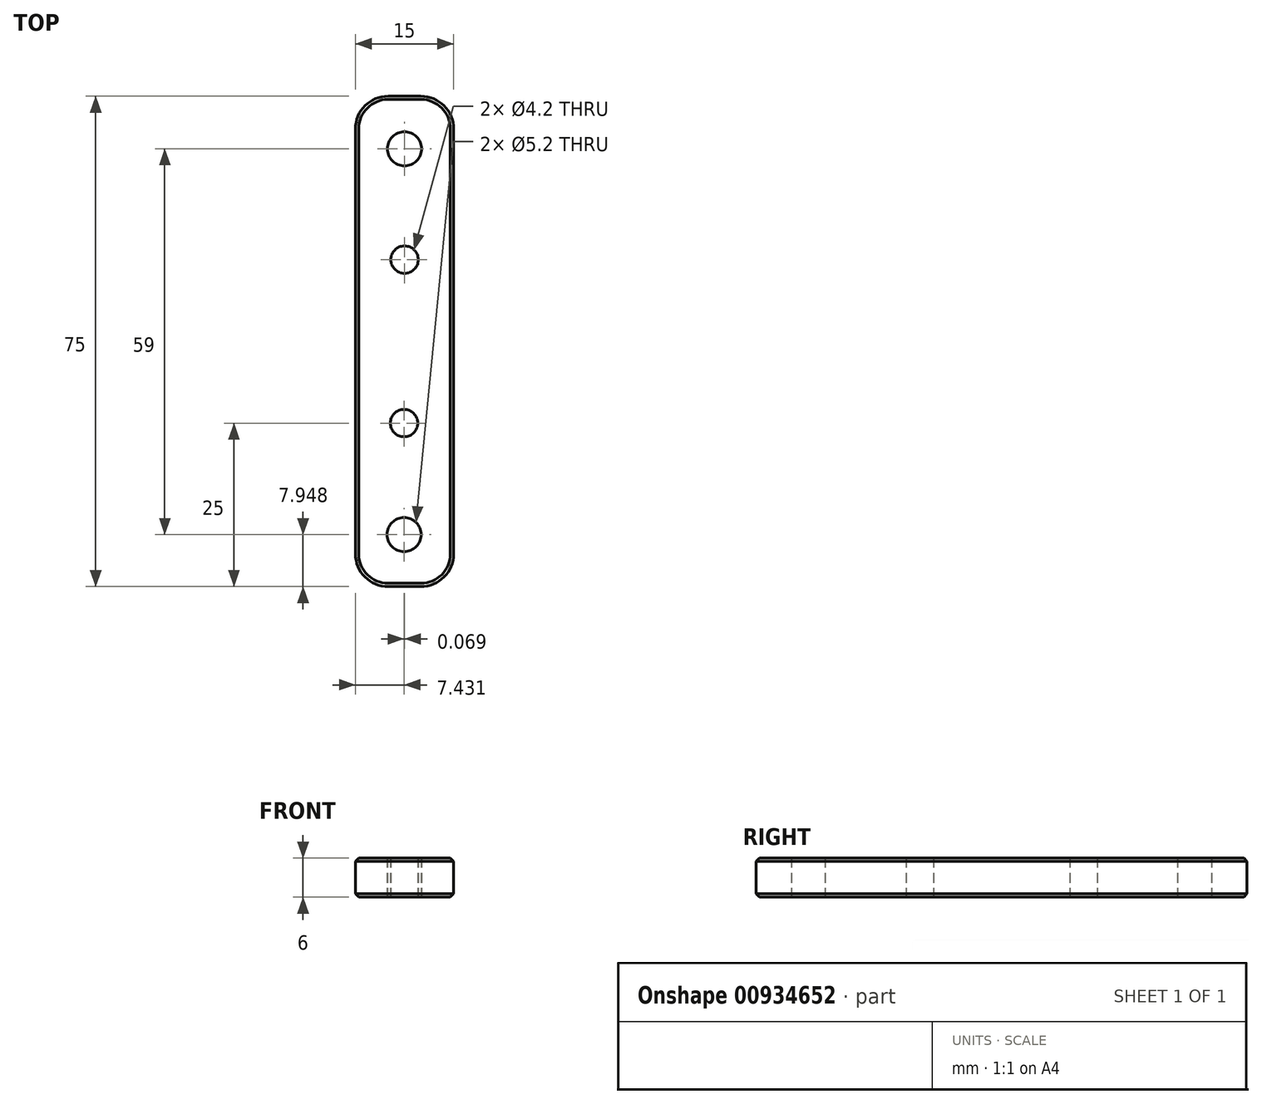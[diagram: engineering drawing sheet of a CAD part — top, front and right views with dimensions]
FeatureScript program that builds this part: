
annotation { "Feature Type Name" : "Feature", "Feature Type Description" : "" }
export const myFeature = defineFeature(function(context is Context, id is Id, definition is map)
    precondition{}
    {
        {
            var Q0;
            Q0=qCreatedBy(makeId("Top.planeOp"),FACE);
            var sketch = newSketch(context, id + "F0", { "sketchPlane" : qUnion([Q0])});
            skLineSegment(sketch, "E0.bottom", {"start": v(-7.5, 37.5) * mm, "end": v(7.5, 37.5) * mm});
            skLineSegment(sketch, "E0.top", {"start": v(-7.5, -37.5) * mm, "end": v(7.5, -37.5) * mm});
            skLineSegment(sketch, "E0.left", {"start": v(-7.5, 37.5) * mm, "end": v(-7.5, -37.5) * mm});
            skLineSegment(sketch, "E0.right", {"start": v(7.5, 37.5) * mm, "end": v(7.5, -37.5) * mm});
            skPoint(sketch, "E0.middle", {"position": v(0, 0) * mm});
            skCircle(sketch, "E1", {"center": v(0, 12.5) * mm, "radius": 2.1 * mm});
            skCircle(sketch, "E2", {"center": v(-0.07, -12.5) * mm, "radius": 2.1 * mm});
            skCircle(sketch, "E3", {"center": v(0, 29.45) * mm, "radius": 2.6 * mm});
            skCircle(sketch, "E4", {"center": v(-0.07, -29.55) * mm, "radius": 2.6 * mm});
            skSolve(sketch);
        }
        {
            var Q0;
            Q0=makeQuery(id+"F0.imprint","IMPRINT",FACE,{"disambiguationData":[TD([[makeQuery(id+"F0.imprint","IMPRINT",EDGE,{"derivedFrom":sQuery(id+"F0.wireOp",EDGE,"E0.bottom")}),-1.0]])]});
            extrude(context, id + "F1", {"entities" : qUnion([Q0]), "depth" : 6 * mm, "offsetDistance" : 25 * mm});
        }
        {
            var Q0;
            Q0=makeQuery(id+"F1.opExtrude","SWEPT_EDGE",EDGE,{"disambiguationData":[OSD([sQuery(id+"F0.wireOp",EDGE,"E0.bottom"),sQuery(id+"F0.wireOp",EDGE,"E0.left")])]});
            var Q1;
            Q1=makeQuery(id+"F1.opExtrude","SWEPT_EDGE",EDGE,{"disambiguationData":[OSD([sQuery(id+"F0.wireOp",EDGE,"E0.bottom"),sQuery(id+"F0.wireOp",EDGE,"E0.right")])]});
            var Q2;
            Q2=makeQuery(id+"F1.opExtrude","SWEPT_EDGE",EDGE,{"disambiguationData":[OSD([sQuery(id+"F0.wireOp",EDGE,"E0.top"),sQuery(id+"F0.wireOp",EDGE,"E0.left")])]});
            var Q3;
            Q3=makeQuery(id+"F1.opExtrude","SWEPT_EDGE",EDGE,{"disambiguationData":[OSD([sQuery(id+"F0.wireOp",EDGE,"E0.top"),sQuery(id+"F0.wireOp",EDGE,"E0.right")])]});
            fillet(context, id + "F2", {"entities" : qUnion([Q0, Q1, Q2, Q3]), "radius" : 5 * mm, "tangentPropagation" : true, "allowEdgeOverflow" : false});
        }
        {
            var Q0;
            Q0=makeQuery(id+"F1.opExtrude","CAP_EDGE",EDGE,{"disambiguationData":[OSD([sQuery(id+"F0.wireOp",EDGE,"E0.left")])],"isStart":false});
            var Q1;
            Q1=makeQuery(id+"F1.opExtrude","CAP_EDGE",EDGE,{"disambiguationData":[OSD([sQuery(id+"F0.wireOp",EDGE,"E0.right")])],"isStart":false});
            var Q2;
            {var subQ0=sQuery(id+"F0.wireOp",EDGE,"E0.right");var subQ1=sQuery(id+"F0.wireOp",EDGE,"E0.bottom");Q2=makeQuery(id+"F2.opFillet","BLEND_EDGE",EDGE,{"blendedFrom":[makeQuery(id+"F1.opExtrude","SWEPT_EDGE",EDGE,{"disambiguationData":[OSD([subQ1,subQ0])]}),makeQuery(id+"F1.opExtrude","CAP_FACE",FACE,{"disambiguationData":[OSD([subQ1,sQuery(id+"F0.wireOp",EDGE,"E0.top"),sQuery(id+"F0.wireOp",EDGE,"E0.left"),subQ0,sQuery(id+"F0.wireOp",EDGE,"E1"),sQuery(id+"F0.wireOp",EDGE,"E2"),sQuery(id+"F0.wireOp",EDGE,"E3"),sQuery(id+"F0.wireOp",EDGE,"E4")])],"isStart":false})],"blendedInto":[makeQuery(id+"F1.opExtrude","CAP_FACE",FACE,{"disambiguationData":[OSD([subQ1,sQuery(id+"F0.wireOp",EDGE,"E0.top"),sQuery(id+"F0.wireOp",EDGE,"E0.left"),subQ0,sQuery(id+"F0.wireOp",EDGE,"E1"),sQuery(id+"F0.wireOp",EDGE,"E2"),sQuery(id+"F0.wireOp",EDGE,"E3"),sQuery(id+"F0.wireOp",EDGE,"E4")])],"isStart":false})]});}
            var Q3;
            Q3=makeQuery(id+"F1.opExtrude","CAP_EDGE",EDGE,{"disambiguationData":[OSD([sQuery(id+"F0.wireOp",EDGE,"E0.bottom")])],"isStart":false});
            var Q4;
            {var subQ0=sQuery(id+"F0.wireOp",EDGE,"E0.left");var subQ1=sQuery(id+"F0.wireOp",EDGE,"E0.bottom");Q4=makeQuery(id+"F2.opFillet","BLEND_EDGE",EDGE,{"blendedFrom":[makeQuery(id+"F1.opExtrude","SWEPT_EDGE",EDGE,{"disambiguationData":[OSD([subQ1,subQ0])]}),makeQuery(id+"F1.opExtrude","CAP_FACE",FACE,{"disambiguationData":[OSD([subQ1,sQuery(id+"F0.wireOp",EDGE,"E0.top"),subQ0,sQuery(id+"F0.wireOp",EDGE,"E0.right"),sQuery(id+"F0.wireOp",EDGE,"E1"),sQuery(id+"F0.wireOp",EDGE,"E2"),sQuery(id+"F0.wireOp",EDGE,"E3"),sQuery(id+"F0.wireOp",EDGE,"E4")])],"isStart":false})],"blendedInto":[makeQuery(id+"F1.opExtrude","CAP_FACE",FACE,{"disambiguationData":[OSD([subQ1,sQuery(id+"F0.wireOp",EDGE,"E0.top"),subQ0,sQuery(id+"F0.wireOp",EDGE,"E0.right"),sQuery(id+"F0.wireOp",EDGE,"E1"),sQuery(id+"F0.wireOp",EDGE,"E2"),sQuery(id+"F0.wireOp",EDGE,"E3"),sQuery(id+"F0.wireOp",EDGE,"E4")])],"isStart":false})]});}
            var Q5;
            {var subQ0=sQuery(id+"F0.wireOp",EDGE,"E0.left");var subQ1=sQuery(id+"F0.wireOp",EDGE,"E0.top");Q5=makeQuery(id+"F2.opFillet","BLEND_EDGE",EDGE,{"blendedFrom":[makeQuery(id+"F1.opExtrude","SWEPT_EDGE",EDGE,{"disambiguationData":[OSD([subQ1,subQ0])]}),makeQuery(id+"F1.opExtrude","CAP_FACE",FACE,{"disambiguationData":[OSD([sQuery(id+"F0.wireOp",EDGE,"E0.bottom"),subQ1,subQ0,sQuery(id+"F0.wireOp",EDGE,"E0.right"),sQuery(id+"F0.wireOp",EDGE,"E1"),sQuery(id+"F0.wireOp",EDGE,"E2"),sQuery(id+"F0.wireOp",EDGE,"E3"),sQuery(id+"F0.wireOp",EDGE,"E4")])],"isStart":false})],"blendedInto":[makeQuery(id+"F1.opExtrude","CAP_FACE",FACE,{"disambiguationData":[OSD([sQuery(id+"F0.wireOp",EDGE,"E0.bottom"),subQ1,subQ0,sQuery(id+"F0.wireOp",EDGE,"E0.right"),sQuery(id+"F0.wireOp",EDGE,"E1"),sQuery(id+"F0.wireOp",EDGE,"E2"),sQuery(id+"F0.wireOp",EDGE,"E3"),sQuery(id+"F0.wireOp",EDGE,"E4")])],"isStart":false})]});}
            var Q6;
            Q6=makeQuery(id+"F1.opExtrude","CAP_EDGE",EDGE,{"disambiguationData":[OSD([sQuery(id+"F0.wireOp",EDGE,"E0.top")])],"isStart":false});
            var Q7;
            {var subQ0=sQuery(id+"F0.wireOp",EDGE,"E0.right");var subQ1=sQuery(id+"F0.wireOp",EDGE,"E0.top");Q7=makeQuery(id+"F2.opFillet","BLEND_EDGE",EDGE,{"blendedFrom":[makeQuery(id+"F1.opExtrude","SWEPT_EDGE",EDGE,{"disambiguationData":[OSD([subQ1,subQ0])]}),makeQuery(id+"F1.opExtrude","CAP_FACE",FACE,{"disambiguationData":[OSD([sQuery(id+"F0.wireOp",EDGE,"E0.bottom"),subQ1,sQuery(id+"F0.wireOp",EDGE,"E0.left"),subQ0,sQuery(id+"F0.wireOp",EDGE,"E1"),sQuery(id+"F0.wireOp",EDGE,"E2"),sQuery(id+"F0.wireOp",EDGE,"E3"),sQuery(id+"F0.wireOp",EDGE,"E4")])],"isStart":false})],"blendedInto":[makeQuery(id+"F1.opExtrude","CAP_FACE",FACE,{"disambiguationData":[OSD([sQuery(id+"F0.wireOp",EDGE,"E0.bottom"),subQ1,sQuery(id+"F0.wireOp",EDGE,"E0.left"),subQ0,sQuery(id+"F0.wireOp",EDGE,"E1"),sQuery(id+"F0.wireOp",EDGE,"E2"),sQuery(id+"F0.wireOp",EDGE,"E3"),sQuery(id+"F0.wireOp",EDGE,"E4")])],"isStart":false})]});}
            var Q8;
            {var subQ0=sQuery(id+"F0.wireOp",EDGE,"E0.left");var subQ1=sQuery(id+"F0.wireOp",EDGE,"E0.bottom");Q8=makeQuery(id+"F2.opFillet","BLEND_EDGE",EDGE,{"blendedFrom":[makeQuery(id+"F1.opExtrude","SWEPT_EDGE",EDGE,{"disambiguationData":[OSD([subQ1,subQ0])]}),makeQuery(id+"F1.opExtrude","CAP_FACE",FACE,{"disambiguationData":[OSD([subQ1,sQuery(id+"F0.wireOp",EDGE,"E0.top"),subQ0,sQuery(id+"F0.wireOp",EDGE,"E0.right"),sQuery(id+"F0.wireOp",EDGE,"E1"),sQuery(id+"F0.wireOp",EDGE,"E2"),sQuery(id+"F0.wireOp",EDGE,"E3"),sQuery(id+"F0.wireOp",EDGE,"E4")])],"isStart":true})],"blendedInto":[makeQuery(id+"F1.opExtrude","CAP_FACE",FACE,{"disambiguationData":[OSD([subQ1,sQuery(id+"F0.wireOp",EDGE,"E0.top"),subQ0,sQuery(id+"F0.wireOp",EDGE,"E0.right"),sQuery(id+"F0.wireOp",EDGE,"E1"),sQuery(id+"F0.wireOp",EDGE,"E2"),sQuery(id+"F0.wireOp",EDGE,"E3"),sQuery(id+"F0.wireOp",EDGE,"E4")])],"isStart":true})]});}
            var Q9;
            Q9=makeQuery(id+"F1.opExtrude","CAP_EDGE",EDGE,{"disambiguationData":[OSD([sQuery(id+"F0.wireOp",EDGE,"E0.bottom")])],"isStart":true});
            var Q10;
            {var subQ0=sQuery(id+"F0.wireOp",EDGE,"E0.right");var subQ1=sQuery(id+"F0.wireOp",EDGE,"E0.bottom");Q10=makeQuery(id+"F2.opFillet","BLEND_EDGE",EDGE,{"blendedFrom":[makeQuery(id+"F1.opExtrude","SWEPT_EDGE",EDGE,{"disambiguationData":[OSD([subQ1,subQ0])]}),makeQuery(id+"F1.opExtrude","CAP_FACE",FACE,{"disambiguationData":[OSD([subQ1,sQuery(id+"F0.wireOp",EDGE,"E0.top"),sQuery(id+"F0.wireOp",EDGE,"E0.left"),subQ0,sQuery(id+"F0.wireOp",EDGE,"E1"),sQuery(id+"F0.wireOp",EDGE,"E2"),sQuery(id+"F0.wireOp",EDGE,"E3"),sQuery(id+"F0.wireOp",EDGE,"E4")])],"isStart":true})],"blendedInto":[makeQuery(id+"F1.opExtrude","CAP_FACE",FACE,{"disambiguationData":[OSD([subQ1,sQuery(id+"F0.wireOp",EDGE,"E0.top"),sQuery(id+"F0.wireOp",EDGE,"E0.left"),subQ0,sQuery(id+"F0.wireOp",EDGE,"E1"),sQuery(id+"F0.wireOp",EDGE,"E2"),sQuery(id+"F0.wireOp",EDGE,"E3"),sQuery(id+"F0.wireOp",EDGE,"E4")])],"isStart":true})]});}
            var Q11;
            Q11=makeQuery(id+"F1.opExtrude","CAP_EDGE",EDGE,{"disambiguationData":[OSD([sQuery(id+"F0.wireOp",EDGE,"E0.right")])],"isStart":true});
            var Q12;
            Q12=makeQuery(id+"F1.opExtrude","CAP_EDGE",EDGE,{"disambiguationData":[OSD([sQuery(id+"F0.wireOp",EDGE,"E0.left")])],"isStart":true});
            var Q13;
            {var subQ0=sQuery(id+"F0.wireOp",EDGE,"E0.left");var subQ1=sQuery(id+"F0.wireOp",EDGE,"E0.top");Q13=makeQuery(id+"F2.opFillet","BLEND_EDGE",EDGE,{"blendedFrom":[makeQuery(id+"F1.opExtrude","SWEPT_EDGE",EDGE,{"disambiguationData":[OSD([subQ1,subQ0])]}),makeQuery(id+"F1.opExtrude","CAP_FACE",FACE,{"disambiguationData":[OSD([sQuery(id+"F0.wireOp",EDGE,"E0.bottom"),subQ1,subQ0,sQuery(id+"F0.wireOp",EDGE,"E0.right"),sQuery(id+"F0.wireOp",EDGE,"E1"),sQuery(id+"F0.wireOp",EDGE,"E2"),sQuery(id+"F0.wireOp",EDGE,"E3"),sQuery(id+"F0.wireOp",EDGE,"E4")])],"isStart":true})],"blendedInto":[makeQuery(id+"F1.opExtrude","CAP_FACE",FACE,{"disambiguationData":[OSD([sQuery(id+"F0.wireOp",EDGE,"E0.bottom"),subQ1,subQ0,sQuery(id+"F0.wireOp",EDGE,"E0.right"),sQuery(id+"F0.wireOp",EDGE,"E1"),sQuery(id+"F0.wireOp",EDGE,"E2"),sQuery(id+"F0.wireOp",EDGE,"E3"),sQuery(id+"F0.wireOp",EDGE,"E4")])],"isStart":true})]});}
            var Q14;
            Q14=makeQuery(id+"F1.opExtrude","CAP_EDGE",EDGE,{"disambiguationData":[OSD([sQuery(id+"F0.wireOp",EDGE,"E0.top")])],"isStart":true});
            var Q15;
            {var subQ0=sQuery(id+"F0.wireOp",EDGE,"E0.right");var subQ1=sQuery(id+"F0.wireOp",EDGE,"E0.top");Q15=makeQuery(id+"F2.opFillet","BLEND_EDGE",EDGE,{"blendedFrom":[makeQuery(id+"F1.opExtrude","SWEPT_EDGE",EDGE,{"disambiguationData":[OSD([subQ1,subQ0])]}),makeQuery(id+"F1.opExtrude","CAP_FACE",FACE,{"disambiguationData":[OSD([sQuery(id+"F0.wireOp",EDGE,"E0.bottom"),subQ1,sQuery(id+"F0.wireOp",EDGE,"E0.left"),subQ0,sQuery(id+"F0.wireOp",EDGE,"E1"),sQuery(id+"F0.wireOp",EDGE,"E2"),sQuery(id+"F0.wireOp",EDGE,"E3"),sQuery(id+"F0.wireOp",EDGE,"E4")])],"isStart":true})],"blendedInto":[makeQuery(id+"F1.opExtrude","CAP_FACE",FACE,{"disambiguationData":[OSD([sQuery(id+"F0.wireOp",EDGE,"E0.bottom"),subQ1,sQuery(id+"F0.wireOp",EDGE,"E0.left"),subQ0,sQuery(id+"F0.wireOp",EDGE,"E1"),sQuery(id+"F0.wireOp",EDGE,"E2"),sQuery(id+"F0.wireOp",EDGE,"E3"),sQuery(id+"F0.wireOp",EDGE,"E4")])],"isStart":true})]});}
            chamfer(context, id + "F3", {"entities" : qUnion([Q0, Q1, Q2, Q3, Q4, Q5, Q6, Q7, Q8, Q9, Q10, Q11, Q12, Q13, Q14, Q15]), "width" : 0.5 * mm, "tangentPropagation" : true});
        }
    });
